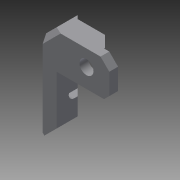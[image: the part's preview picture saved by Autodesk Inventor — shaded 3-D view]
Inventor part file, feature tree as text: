
AUTODESK INVENTOR PART (.ipt)
format: ipt  version: 2015 (Build 190159000, 159)  size: 178,688 bytes
history: native  units: mm
features: sketch x7, chamfer x6, extrude x5, hole x2
ambient origin geometry x8: Origin, YZ Plane, XZ Plane, XY Plane, X Axis, Y Axis, Z Axis, Center Point
bodies: Solid1 (feature_tree)
feature tree (20):
  extrude  "Extrusion1"  Depth=38.0mm
  extrude  "Extrusion2"  Depth=8.0mm
  extrude  "Extrusion3"  Depth=16.0mm TaperAngle=0.0deg
  extrude  "Extrusion4"  Depth=11.0mm
  chamfer  "Chamfer1"  Distance=5.0mm
  chamfer  "Chamfer2"  Distance=7.0mm
  chamfer  "Chamfer3"  Distance=15.5mm
  chamfer  "Chamfer4"  Distance=8.0mm
  chamfer  "Chamfer5"  Distance=4.0mm
  chamfer  "Chamfer6"  Distance=11.0mm
  hole  "Hole1"  [1 undecoded]
  extrude  "Extrusion5"  Depth=7.0mm TaperAngle=45.0deg
  hole  "Hole2"  [1 undecoded]
  sketch  "Sketch1"  dims[d0=38.0mm d1=55.0mm]
  sketch  "Sketch2"  dims[d2=16.0mm d3=0.0mm d4=8.0mm]
  sketch  "Sketch3"  dims[d5=20.0mm d6=16.0mm d7=0.0mm]
  sketch  "Sketch4"  dims[d8=5.0mm d9=11.0mm]
  sketch  "Sketch5"  dims[d10=0.0mm]
  sketch  "Sketch6"  dims[d11=0.5mm]
  sketch  "Sketch7"  dims[d12=8.0mm d13=5.0mm d16=7.0mm d17=15.5mm d18=8.0mm d19=4.0mm d20=11.0mm d21=0.0mm d22=7.0mm d23=7.0mm d24=45.0deg d25=6.0mm d26=6.0mm d27=45.0deg d28=1.0mm d29=1.0mm d30=45.0deg d31=5.0mm d32=5.0mm d33=45.0deg d34=3.0mm d35=3.0mm d36=45.0deg d37=2.0mm d38=3.0mm d39=45.0deg d40=6.0mm d41=20.0mm d45=10.0mm d46=3.6mm d47=6.0mm d48=6.2mm d49=4.0mm d50=90.0deg d51=8.0mm d52=20.594885mm d53=6.2mm d54=6.2mm d55=20.0mm d56=4.0mm d57=10.0mm d58=6.0mm d59=0.0mm d60=13.0mm d61=10.8mm d62=8.0mm d63=6.0mm d64=6.2mm d65=4.0mm d66=90.0deg d67=8.0mm d68=20.594885mm]
note: 2 required parameter values undecoded (feature->parameter linkage not recoverable at this tier; creation-order binding heuristic only, values carry confidence <= 0.55)
